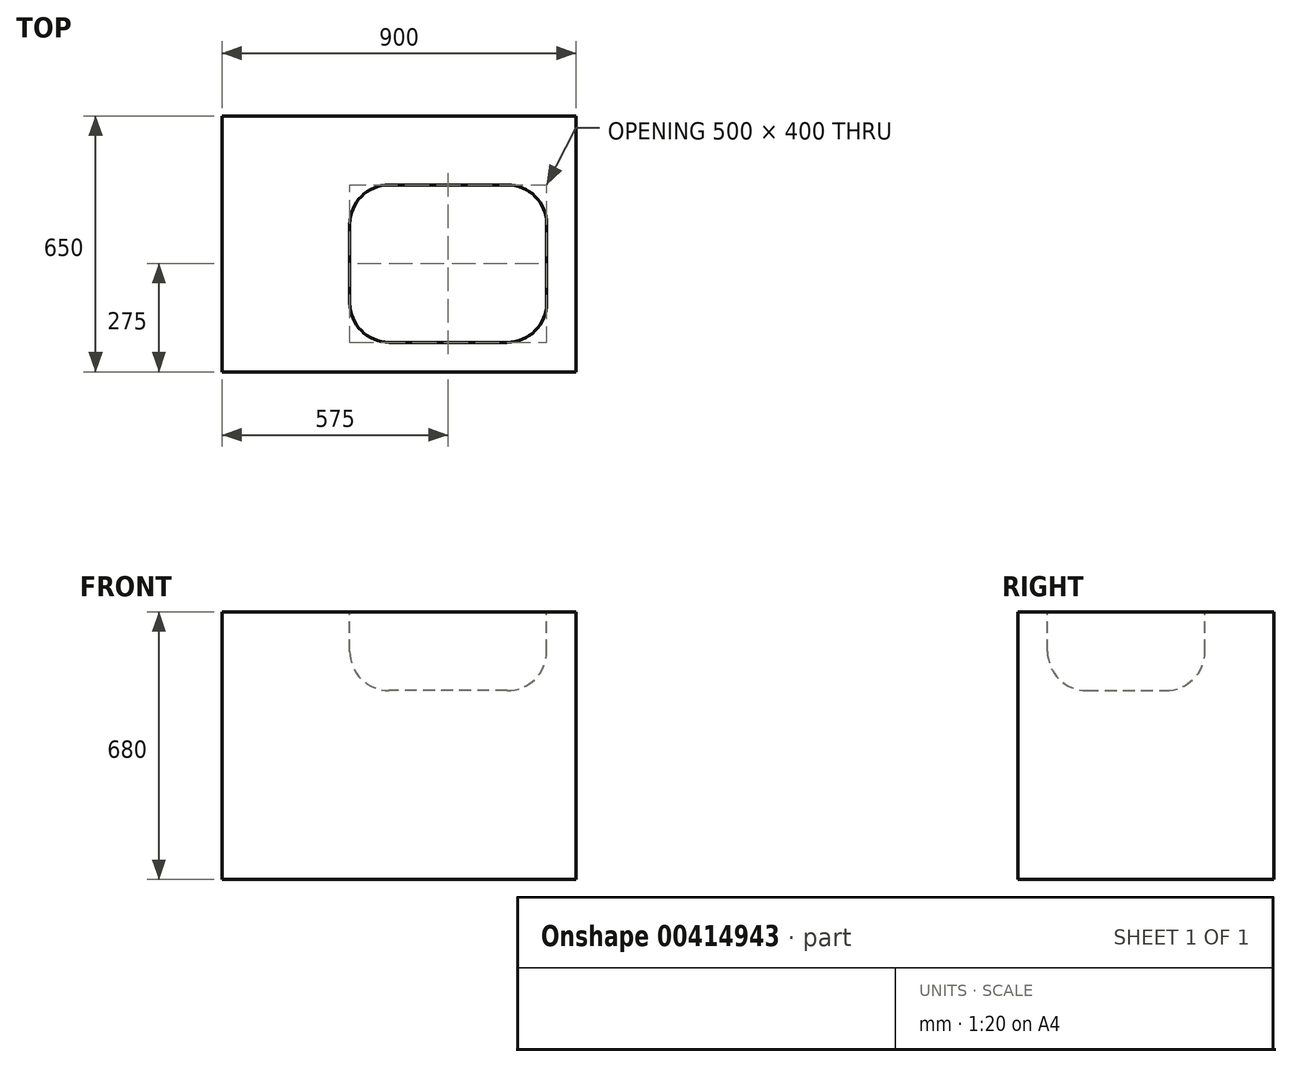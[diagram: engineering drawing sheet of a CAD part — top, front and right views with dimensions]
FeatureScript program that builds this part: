
annotation { "Feature Type Name" : "Feature", "Feature Type Description" : "" }
export const myFeature = defineFeature(function(context is Context, id is Id, definition is map)
    precondition{}
    {
        {
            var Q0;
            Q0=qCreatedBy(makeId("Top.planeOp"),FACE);
            var sketch = newSketch(context, id + "F0", { "sketchPlane" : qUnion([Q0])});
            skLineSegment(sketch, "E0.bottom", {"start": v(0, 0) * mm, "end": v(900, 0) * mm});
            skLineSegment(sketch, "E0.top", {"start": v(0, 650) * mm, "end": v(900, 650) * mm});
            skLineSegment(sketch, "E0.left", {"start": v(0, 0) * mm, "end": v(0, 650) * mm});
            skLineSegment(sketch, "E0.right", {"start": v(900, 0) * mm, "end": v(900, 650) * mm});
            skSolve(sketch);
        }
        {
            var Q0;
            Q0 = qSketchRegion(id + "F0", true);
            extrude(context, id + "F1", {"entities" : qUnion([Q0]), "depth" : 680 * mm});
        }
        {
            var Q0;
            Q0=makeQuery(id+"F1.opExtrude","CAP_FACE",FACE,{"disambiguationData":[OSD([sQuery(id+"F0.wireOp",EDGE,"E0.bottom"),sQuery(id+"F0.wireOp",EDGE,"E0.top"),sQuery(id+"F0.wireOp",EDGE,"E0.left"),sQuery(id+"F0.wireOp",EDGE,"E0.right")])],"isStart":false});
            var sketch = newSketch(context, id + "F2", { "sketchPlane" : qUnion([Q0])});
            skLineSegment(sketch, "E1.bottom", {"start": v(825, 75) * mm, "end": v(325, 75) * mm});
            skLineSegment(sketch, "E1.top", {"start": v(825, 475) * mm, "end": v(325, 475) * mm});
            skLineSegment(sketch, "E1.left", {"start": v(825, 75) * mm, "end": v(825, 475) * mm});
            skLineSegment(sketch, "E1.right", {"start": v(325, 75) * mm, "end": v(325, 475) * mm});
            skSolve(sketch);
        }
        {
            var Q0;
            Q0 = qSketchRegion(id + "F2", true);
            extrude(context, id + "F3", {"entities" : qUnion([Q0]), "operationType" : NewBodyOperationType.REMOVE, "oppositeDirection" : true, "depth" : 200 * mm});
        }
        {
            var Q0;
            Q0=makeQuery(id+"F3.boolean.opBoolean","COPY",EDGE,{"derivedFrom":makeQuery(id+"F3.opExtrude","CAP_EDGE",EDGE,{"disambiguationData":[OSD([sQuery(id+"F2.wireOp",EDGE,"E1.right")])],"isStart":false})});
            var Q1;
            Q1=makeQuery(id+"F3.boolean.opBoolean","COPY",EDGE,{"derivedFrom":makeQuery(id+"F3.opExtrude","CAP_EDGE",EDGE,{"disambiguationData":[OSD([sQuery(id+"F2.wireOp",EDGE,"E1.top")])],"isStart":false})});
            var Q2;
            Q2=makeQuery(id+"F3.boolean.opBoolean","COPY",EDGE,{"derivedFrom":makeQuery(id+"F3.opExtrude","SWEPT_EDGE",EDGE,{"disambiguationData":[OSD([sQuery(id+"F2.wireOp",EDGE,"E1.top"),sQuery(id+"F2.wireOp",EDGE,"E1.right")])]})});
            var Q3;
            Q3=makeQuery(id+"F3.boolean.opBoolean","COPY",EDGE,{"derivedFrom":makeQuery(id+"F3.opExtrude","SWEPT_EDGE",EDGE,{"disambiguationData":[OSD([sQuery(id+"F2.wireOp",EDGE,"E1.top"),sQuery(id+"F2.wireOp",EDGE,"E1.left")])]})});
            var Q4;
            Q4=makeQuery(id+"F3.boolean.opBoolean","COPY",EDGE,{"derivedFrom":makeQuery(id+"F3.opExtrude","SWEPT_EDGE",EDGE,{"disambiguationData":[OSD([sQuery(id+"F2.wireOp",EDGE,"E1.bottom"),sQuery(id+"F2.wireOp",EDGE,"E1.left")])]})});
            var Q5;
            Q5=makeQuery(id+"F3.boolean.opBoolean","COPY",EDGE,{"derivedFrom":makeQuery(id+"F3.opExtrude","CAP_EDGE",EDGE,{"disambiguationData":[OSD([sQuery(id+"F2.wireOp",EDGE,"E1.left")])],"isStart":false})});
            var Q6;
            Q6=makeQuery(id+"F3.boolean.opBoolean","COPY",EDGE,{"derivedFrom":makeQuery(id+"F3.opExtrude","CAP_EDGE",EDGE,{"disambiguationData":[OSD([sQuery(id+"F2.wireOp",EDGE,"E1.bottom")])],"isStart":false})});
            var Q7;
            Q7=makeQuery(id+"F3.boolean.opBoolean","COPY",EDGE,{"derivedFrom":makeQuery(id+"F3.opExtrude","SWEPT_EDGE",EDGE,{"disambiguationData":[OSD([sQuery(id+"F2.wireOp",EDGE,"E1.bottom"),sQuery(id+"F2.wireOp",EDGE,"E1.right")])]})});
            fillet(context, id + "F4", {"entities" : qUnion([Q0, Q1, Q2, Q3, Q4, Q5, Q6, Q7]), "radius" : 100 * mm, "tangentPropagation" : true, "allowEdgeOverflow" : false});
        }
    });
